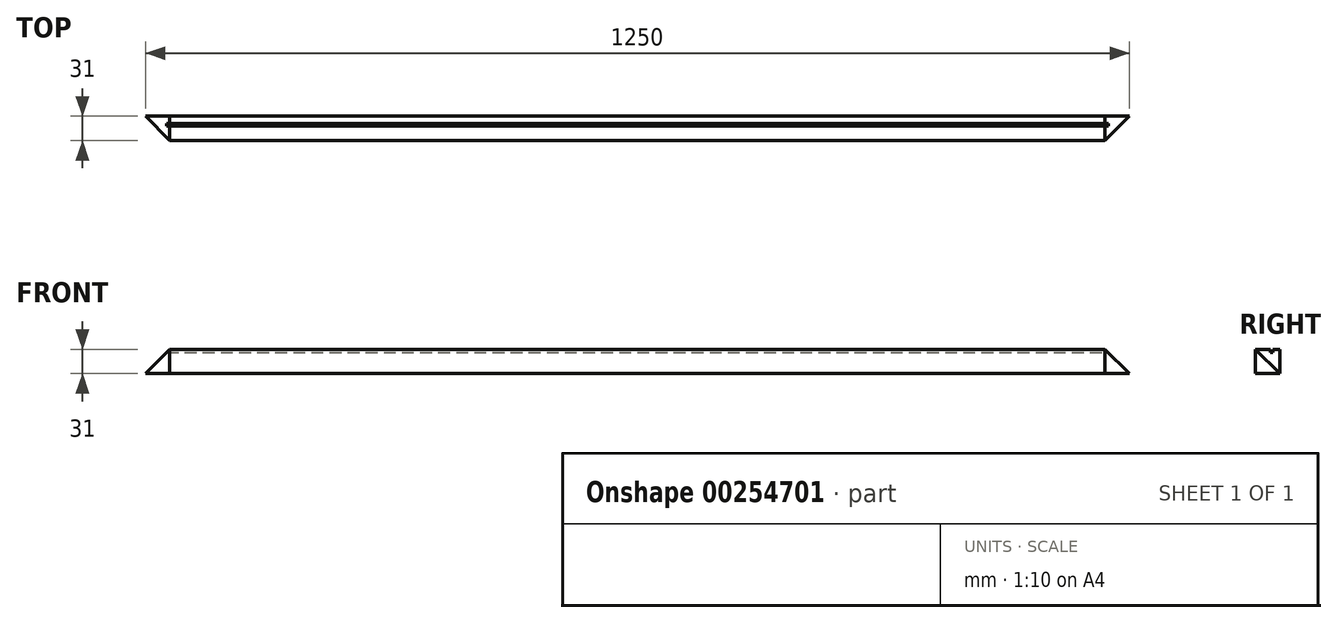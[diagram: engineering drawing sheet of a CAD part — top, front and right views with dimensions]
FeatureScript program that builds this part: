
annotation { "Feature Type Name" : "Feature", "Feature Type Description" : "" }
export const myFeature = defineFeature(function(context is Context, id is Id, definition is map)
    precondition{}
    {
        {
            var Q0;
            Q0=qCreatedBy(makeId("Top.planeOp"),FACE);
            var sketch = newSketch(context, id + "F0", { "sketchPlane" : qUnion([Q0])});
            skLineSegment(sketch, "E0.bottom", {"start": v(31, 0) * mm, "end": v(1219, 0) * mm});
            skLineSegment(sketch, "E0.top", {"start": v(0, 31) * mm, "end": v(1250, 31) * mm});
            skLineSegment(sketch, "E1", {"start": v(0, 31) * mm, "end": v(31, 0) * mm});
            skLineSegment(sketch, "E2", {"start": v(625, 31) * mm, "end": v(625, 0) * mm, "construction": true});
            skLineSegment(sketch, "E3.MirrorCS", {"start": v(1250, 31) * mm, "end": v(1219, 0) * mm});
            skSolve(sketch);
        }
        {
            var Q0;
            Q0=qSketchRegion(id+"F0",true);
            extrude(context, id + "F1", {"entities" : qUnion([Q0]), "depth" : 31 * mm});
        }
        {
            var Q0;
            Q0=makeQuery(id+"F1.opExtrude","SWEPT_FACE",FACE,{"disambiguationData":[OSD([sQuery(id+"F0.wireOp",EDGE,"E0.top")])]});
            var sketch = newSketch(context, id + "F2", { "sketchPlane" : qUnion([Q0])});
            skLineSegment(sketch, "E4", {"start": v(0, 0) * mm, "end": v(0, 31) * mm});
            skLineSegment(sketch, "E5", {"start": v(0, 31) * mm, "end": v(-31, 31) * mm});
            skLineSegment(sketch, "E6", {"start": v(-31, 31) * mm, "end": v(0, 0) * mm});
            skLineSegment(sketch, "E7", {"start": v(-625, 31) * mm, "end": v(-625, 0) * mm, "construction": true});
            skLineSegment(sketch, "E8.MirrorCS", {"start": v(-1219, 31) * mm, "end": v(-1250, 0) * mm});
            skLineSegment(sketch, "E9.MirrorCS", {"start": v(-1250, 0) * mm, "end": v(-1250, 31) * mm});
            skLineSegment(sketch, "E10.MirrorCS", {"start": v(-1250, 31) * mm, "end": v(-1219, 31) * mm});
            skSolve(sketch);
        }
        {
            var Q0;
            Q0=qSketchRegion(id+"F2",true);
            extrude(context, id + "F3", {"entities" : qUnion([Q0]), "operationType" : NewBodyOperationType.REMOVE, "endBound" : BoundingType.THROUGH_ALL, "oppositeDirection" : true, "depth" : 25 * mm});
        }
        {
            var Q0;
            Q0=makeQuery(id+"F1.opExtrude","CAP_FACE",FACE,{"disambiguationData":[OSD([sQuery(id+"F0.wireOp",EDGE,"E0.bottom"),sQuery(id+"F0.wireOp",EDGE,"E0.top"),sQuery(id+"F0.wireOp",EDGE,"E1"),sQuery(id+"F0.wireOp",EDGE,"E3.MirrorCS")])],"isStart":false});
            var sketch = newSketch(context, id + "F4", { "sketchPlane" : qUnion([Q0])});
            skPoint(sketch, "E11.oppositeSnap0", {"position": v(1219, 15.5) * mm});
            skLineSegment(sketch, "E12.bottom", {"start": v(27, 22) * mm, "end": v(1223, 22) * mm});
            skLineSegment(sketch, "E12.top", {"start": v(27, 18.8) * mm, "end": v(1223, 18.8) * mm});
            skLineSegment(sketch, "E12.left", {"start": v(27, 22) * mm, "end": v(27, 18.8) * mm});
            skLineSegment(sketch, "E12.right", {"start": v(1223, 22) * mm, "end": v(1223, 18.8) * mm});
            skLineSegment(sketch, "E13", {"start": v(625, 22) * mm, "end": v(625, 18.8) * mm, "construction": true});
            skSolve(sketch);
        }
        {
            var Q0;
            Q0=qSketchRegion(id+"F4",true);
            extrude(context, id + "F5", {"entities" : qUnion([Q0]), "operationType" : NewBodyOperationType.REMOVE, "oppositeDirection" : true, "depth" : 4 * mm});
        }
    });
